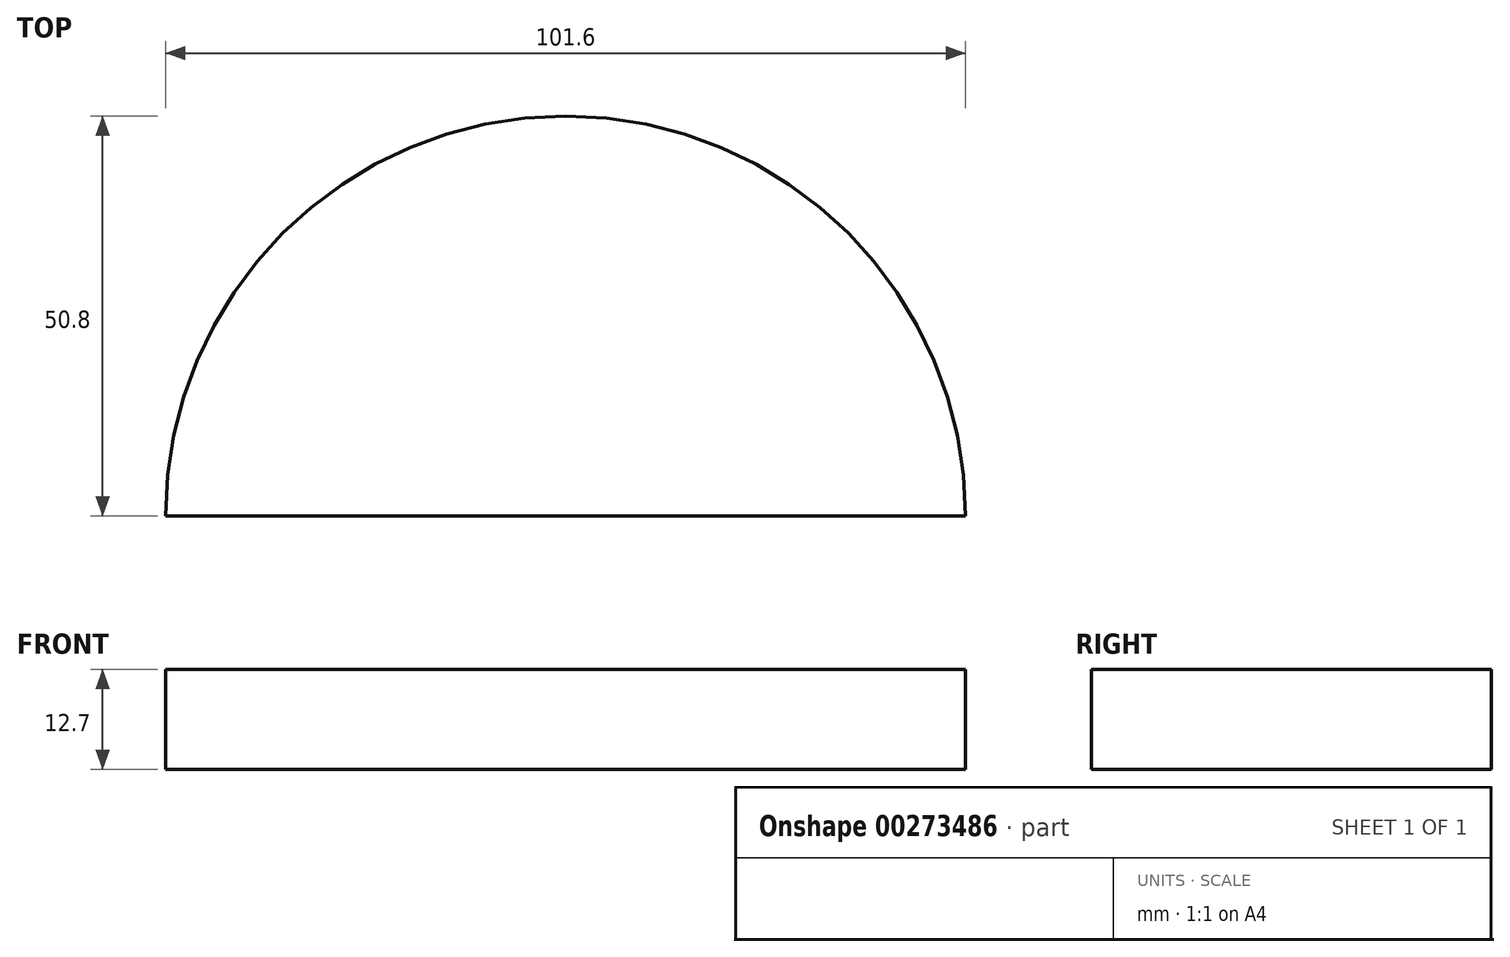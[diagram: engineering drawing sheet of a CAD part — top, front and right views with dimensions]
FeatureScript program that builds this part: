
annotation { "Feature Type Name" : "Feature", "Feature Type Description" : "" }
export const myFeature = defineFeature(function(context is Context, id is Id, definition is map)
    precondition{}
    {
        {
            var Q0;
            Q0=qCreatedBy(makeId("Top.planeOp"),FACE);
            var sketch = newSketch(context, id + "F0", { "sketchPlane" : qUnion([Q0])});
            skArc(sketch, "E0", {"start": v(50.8, 0) * mm, "mid": v(0, 50.8) * mm, "end": v(-50.8, 0) * mm});
            skLineSegment(sketch, "E1", {"start": v(-50.8, 0) * mm, "end": v(50.8, 0) * mm});
            skSolve(sketch);
        }
        {
            var Q0;
            Q0 = qSketchRegion(id + "F0", true);
            extrude(context, id + "F1", {"entities" : qUnion([Q0]), "depth" : 12.7 * mm});
        }
    });
